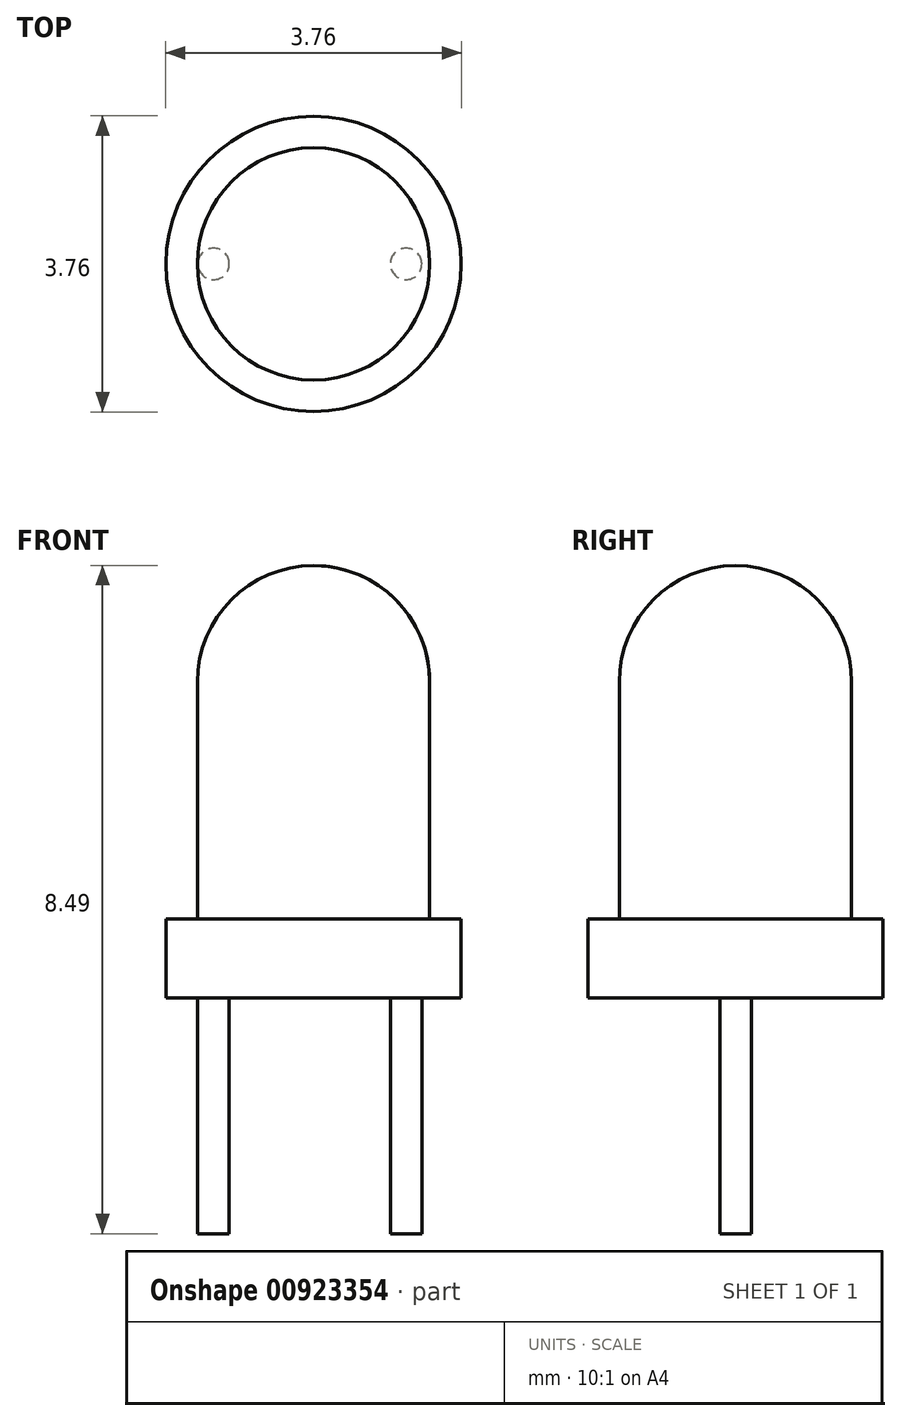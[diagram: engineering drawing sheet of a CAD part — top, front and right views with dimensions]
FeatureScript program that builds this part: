
annotation { "Feature Type Name" : "Feature", "Feature Type Description" : "" }
export const myFeature = defineFeature(function(context is Context, id is Id, definition is map)
    precondition{}
    {
        {
            var Q0;
            Q0=qCreatedBy(makeId("Front.planeOp"),FACE);
            var sketch = newSketch(context, id + "F0", { "sketchPlane" : qUnion([Q0])});
            skArc(sketch, "E0", {"start": v(0, 5.34) * mm, "mid": v(-1.04, 4.9) * mm, "end": v(-1.48, 3.86) * mm});
            skLineSegment(sketch, "E1", {"start": v(-1.48, 3.86) * mm, "end": v(-1.48, 0.85) * mm});
            skLineSegment(sketch, "E2", {"start": v(0, 5.34) * mm, "end": v(0, -0.15) * mm});
            skLineSegment(sketch, "E3", {"start": v(-1.47, 0.85) * mm, "end": v(-1.87, 0.85) * mm});
            skLineSegment(sketch, "E4", {"start": v(-1.87, 0.85) * mm, "end": v(-1.87, -0.15) * mm});
            skLineSegment(sketch, "E5", {"start": v(-1.87, -0.15) * mm, "end": v(0, -0.15) * mm});
            skSolve(sketch);
        }
        {
            var Q0;
            Q0=qSketchRegion(id+"F0",true);
            var Q1;
            Q1=sQuery(id+"F0.wireOp",EDGE,"E2");
            revolve(context, id + "F1", {"surfaceOperationType" : NewSurfaceOperationType.NEW, "entities" : qUnion([Q0]), "axis" : qUnion([Q1]), "revolveType" : RevolveType.FULL});
        }
        {
            var Q0;
            Q0=makeQuery(id+"F1.opRevolve","SWEPT_FACE",FACE,{"disambiguationData":[OSD([sQuery(id+"F0.wireOp",EDGE,"E5")])]});
            var sketch = newSketch(context, id + "F2", { "sketchPlane" : qUnion([Q0])});
            skCircle(sketch, "E6", {"center": v(-1.27, 0) * mm, "radius": 0.2 * mm});
            skCircle(sketch, "E7", {"center": v(1.18, 0) * mm, "radius": 0.2 * mm});
            skSolve(sketch);
        }
        {
            var Q0;
            Q0=qSketchRegion(id+"F2",true);
            extrude(context, id + "F3", {"entities" : qUnion([Q0]), "depth" : 3 * mm, "offsetDistance" : 25 * mm});
        }
    });
